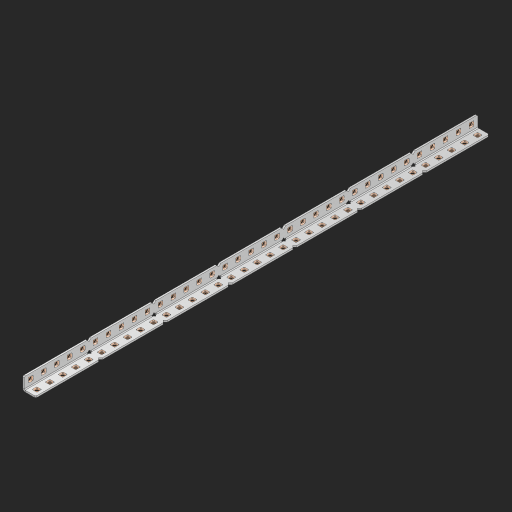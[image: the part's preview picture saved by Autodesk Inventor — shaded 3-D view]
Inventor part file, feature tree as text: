
AUTODESK INVENTOR PART (.ipt)
format: ipt  version: 2023 (Build 270158000, 158)  size: 1,129,984 bytes
history: native  units: in
note: dims shown in document units (in); Inventor stores cm internally (conversion verified against a paired STEP export)
features: other x76, extrude x71, sheet_metal_op x8, sketch x5, pattern_linear x1, mirror x1, chamfer x1
ambient origin geometry x8: Origin, YZ Plane, XZ Plane, XY Plane, X Axis, Y Axis, Z Axis, Center Point
bodies: Solid1 (feature_tree), Body (feature_tree)
feature tree (163):
  sheet_metal_op  "Flanges"
  sheet_metal_op  "Body Pattern"
  other  "Arc Length"
  pattern_linear  "Notch Pattern"  Spacing1=0.125in  [1 undecoded]
  other  "Diagonal Plane"
  mirror  "Everything Mirrored"
  chamfer  "End Chamfer"
  sketch  "Sketch1"  dims[d0=0.5in]
  other  "Plate1"
  sketch  "Sketch2"  dims[d1=17.5in]
  other  "Plate2"
  sheet_metal_op  "Bend1"
  sheet_metal_op  "Corner1"
  sketch  "Sketch8"  dims[d2=0.0625in]
  sketch  "Sketch9"  dims[d3=0.0625in]
  other  "Srf91"
  sheet_metal_op  "Body Pattern Sketch"
  other  "Srf92"
  sketch  "Sketch13"  dims[d4=0.0312in d5=0.125in d6=0.0625in d7=0.5in d8=90.0deg d9=0.0312in d10=0.25in d11=0.0625in d12=0.0625in d49=0.182in d50=0.02in d52=0.25in d53=0.0625in d54=0.0in d55=0.172in d56=1.0in d57=0.0in d85=0.1473in d86=0.1782in d89=0.0625in d90=0.0in d91=0.04in d92=0.0491in d95=2.5in d96=0.04in d97=0.25in d98=45.0deg d123=0.204in d126=0.0491in d127=0.1473in d128=0.08in d129=0.04in d130=2.5in d131=13.7795in d133=0.5in d134=0.3937in d136=1.0in]
  other  "Srf856"
  other  "Srf857"
  other  "Srf858"
  other  "Srf859"
  other  "Srf860"
  other  "Srf861"
  other  "Srf1275"
  other  "Srf1276"
  other  "Srf1278"
  other  "Srf1279"
  other  "Srf1280"
  other  "Srf1281"
  other  "Srf1282"
  other  "Srf1283"
  other  "Srf1383"
  other  "Srf1384"
  other  "Srf1385"
  other  "Srf1386"
  other  "Srf1387"
  other  "Srf1388"
  other  "Srf1389"
  other  "Srf1390"
  other  "Srf1391"
  other  "Srf1392"
  other  "Srf1393"
  other  "Srf1394"
  other  "Srf1395"
  other  "Srf1396"
  other  "Srf1397"
  other  "Srf1398"
  other  "Srf1399"
  other  "Srf1400"
  other  "Srf1401"
  other  "Srf1402"
  other  "Srf1403"
  other  "Srf1404"
  other  "Srf1405"
  other  "Srf1406"
  other  "Srf1407"
  other  "Srf1408"
  other  "Srf1409"
  other  "Srf1475"
  other  "Srf1476"
  other  "Srf1477"
  other  "Srf1478"
  other  "Srf1479"
  other  "Srf1480"
  other  "Srf1481"
  other  "Srf1482"
  other  "Srf1483"
  other  "Srf1484"
  other  "Srf1485"
  other  "Srf1486"
  other  "Srf1487"
  other  "Srf1488"
  other  "Srf1489"
  other  "Srf1490"
  other  "Srf1491"
  other  "Srf1492"
  other  "Srf1493"
  other  "Srf1494"
  other  "Srf1495"
  other  "Srf1496"
  other  "Srf1497"
  other  "Srf1498"
  other  "Srf1499"
  other  "Srf1500"
  other  "Srf1501"
  other  "Srf1568"
  other  "Srf1569"
  sheet_metal_op  "Body Stamp"
  sheet_metal_op  "Body Circle"
  sheet_metal_op  "Notch"
  extrude  "ExtrusionSrf92"  Depth=0.0625in
  extrude  "ExtrusionSrf856"  Depth=0.5in TaperAngle=90.0deg
  extrude  "ExtrusionSrf857"  Depth=0.25in
  extrude  "ExtrusionSrf858"  Depth=0.0625in
  extrude  "ExtrusionSrf859"  Depth=0.0625in
  extrude  "ExtrusionSrf860"  Depth=0.3937in
  extrude  "ExtrusionSrf861"  Depth=0.02in
  extrude  "ExtrusionSrf1275"  Depth=0.25in
  extrude  "ExtrusionSrf1276"  Depth=0.0625in
  extrude  "ExtrusionSrf1277"  TaperAngle=0.0deg  [1 undecoded]
  extrude  "ExtrusionSrf1278"  Depth=0.3937in
  extrude  "ExtrusionSrf1279"  Depth=0.3937in TaperAngle=0.0deg
  extrude  "ExtrusionSrf1280"  Depth=0.3937in
  extrude  "ExtrusionSrf1281"  Depth=0.3937in
  extrude  "ExtrusionSrf1282"  Depth=0.0625in
  extrude  "ExtrusionSrf1383"  Depth=0.3937in TaperAngle=0.0deg
  extrude  "ExtrusionSrf1384"  Depth=0.3937in
  extrude  "ExtrusionSrf1385"  Depth=0.25in TaperAngle=45.0deg
  extrude  "ExtrusionSrf1386"  Depth=0.3937in
  extrude  "ExtrusionSrf1387"  Depth=0.3937in
  extrude  "ExtrusionSrf1388"  Depth=0.3937in
  extrude  "ExtrusionSrf1389"  Depth=0.3937in
  extrude  "ExtrusionSrf1390"  Depth=0.3937in
  extrude  "ExtrusionSrf1391"  Depth=0.3937in
  extrude  "ExtrusionSrf1392"  Depth=0.3937in
  extrude  "ExtrusionSrf1393"  Depth=0.5in
  extrude  "ExtrusionSrf1394"  [1 undecoded]
  extrude  "ExtrusionSrf1395"  [1 undecoded]
  extrude  "ExtrusionSrf1396"  [1 undecoded]
  extrude  "ExtrusionSrf1397"  [1 undecoded]
  extrude  "ExtrusionSrf1398"  [1 undecoded]
  extrude  "ExtrusionSrf1399"  [1 undecoded]
  extrude  "ExtrusionSrf1400"  [1 undecoded]
  extrude  "ExtrusionSrf1401"  [1 undecoded]
  extrude  "ExtrusionSrf1402"  [1 undecoded]
  extrude  "ExtrusionSrf1403"  [1 undecoded]
  extrude  "ExtrusionSrf1404"  [1 undecoded]
  extrude  "ExtrusionSrf1405"  [1 undecoded]
  extrude  "ExtrusionSrf1406"  [1 undecoded]
  extrude  "ExtrusionSrf1407"  [1 undecoded]
  extrude  "ExtrusionSrf1408"  [1 undecoded]
  extrude  "ExtrusionSrf1409"  [1 undecoded]
  extrude  "ExtrusionSrf1475"  [1 undecoded]
  extrude  "ExtrusionSrf1476"  [1 undecoded]
  extrude  "ExtrusionSrf1477"  [1 undecoded]
  extrude  "ExtrusionSrf1478"  [1 undecoded]
  extrude  "ExtrusionSrf1479"  [1 undecoded]
  extrude  "ExtrusionSrf1480"  [1 undecoded]
  extrude  "ExtrusionSrf1481"  [1 undecoded]
  extrude  "ExtrusionSrf1482"  [1 undecoded]
  extrude  "ExtrusionSrf1483"  [1 undecoded]
  extrude  "ExtrusionSrf1484"  [1 undecoded]
  extrude  "ExtrusionSrf1485"  [1 undecoded]
  extrude  "ExtrusionSrf1486"  [1 undecoded]
  extrude  "ExtrusionSrf1487"  [1 undecoded]
  extrude  "ExtrusionSrf1488"  [1 undecoded]
  extrude  "ExtrusionSrf1489"  [1 undecoded]
  extrude  "ExtrusionSrf1490"  [1 undecoded]
  extrude  "ExtrusionSrf1491"  [1 undecoded]
  extrude  "ExtrusionSrf1492"  [1 undecoded]
  extrude  "ExtrusionSrf1493"  [1 undecoded]
  extrude  "ExtrusionSrf1494"  [1 undecoded]
  extrude  "ExtrusionSrf1495"  [1 undecoded]
  extrude  "ExtrusionSrf1496"  [1 undecoded]
  extrude  "ExtrusionSrf1497"  [1 undecoded]
  extrude  "ExtrusionSrf1498"  [1 undecoded]
  extrude  "ExtrusionSrf1499"  [1 undecoded]
  extrude  "ExtrusionSrf1500"  [1 undecoded]
  extrude  "ExtrusionSrf1501"  [1 undecoded]
  extrude  "ExtrusionSrf1568"  [1 undecoded]
  extrude  "ExtrusionSrf1569"  [1 undecoded]
note: 47 required parameter values undecoded (feature->parameter linkage not recoverable at this tier; creation-order binding heuristic only, values carry confidence <= 0.55)
